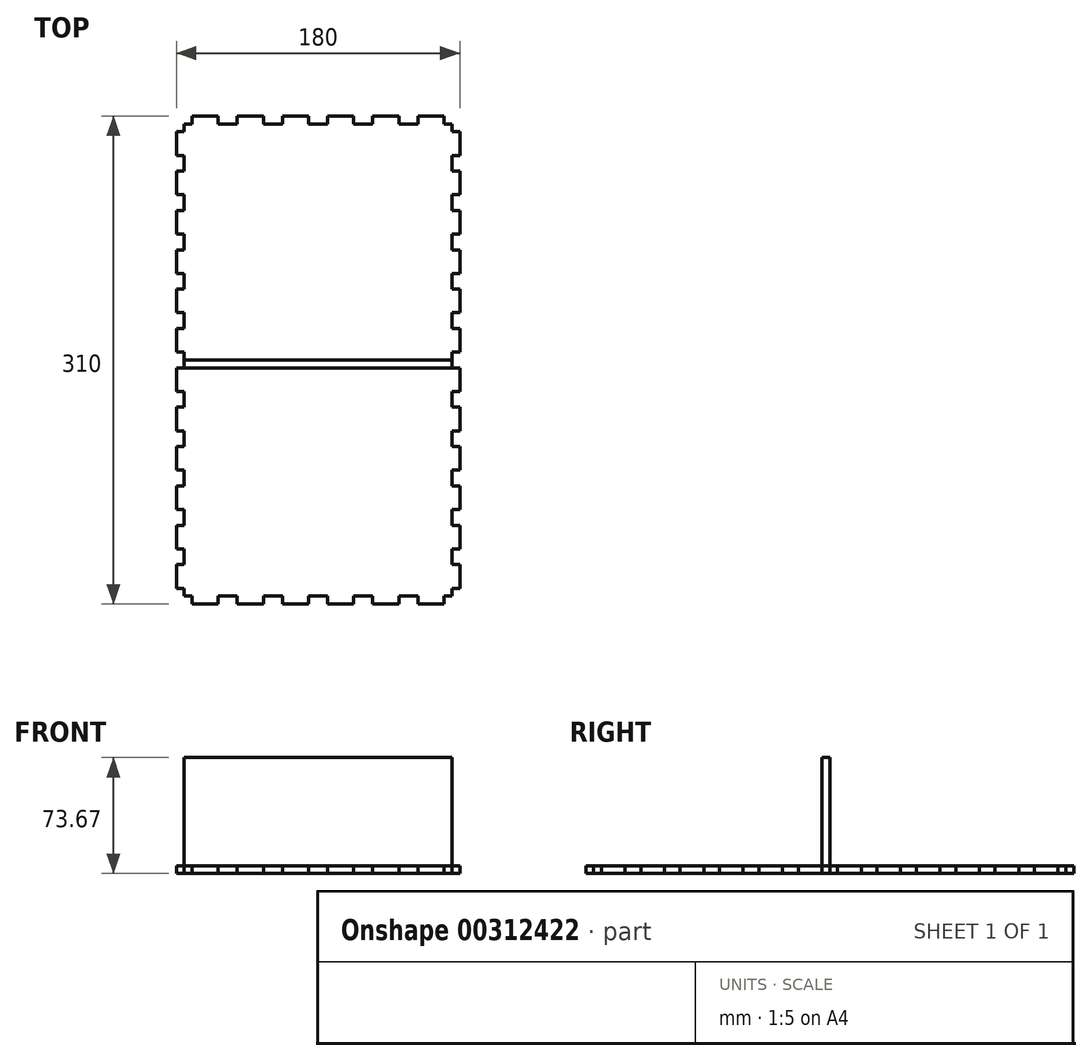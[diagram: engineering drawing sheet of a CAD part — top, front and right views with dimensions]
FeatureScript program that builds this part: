
annotation { "Feature Type Name" : "Feature", "Feature Type Description" : "" }
export const myFeature = defineFeature(function(context is Context, id is Id, definition is map)
    precondition{}
    {
        {
            assignVariable(context, id + "F0", {"name" : "Materialthickness", "anyValue" : 5});
        }
        {
            var Q0;
            Q0=qCreatedBy(makeId("Top.planeOp"),FACE);
            var sketch = newSketch(context, id + "F1", { "sketchPlane" : qUnion([Q0])});
            skLineSegment(sketch, "E0.top", {"start": v(-85, -150) * mm, "end": v(-80, -150) * mm});
            skLineSegment(sketch, "E0.left", {"start": v(-85, 150) * mm, "end": v(-85, 145) * mm});
            skLineSegment(sketch, "E0.right", {"start": v(85, 150) * mm, "end": v(85, 145) * mm});
            skLineSegment(sketch, "E1", {"start": v(0, 150) * mm, "end": v(0, -150) * mm, "construction": true});
            skLineSegment(sketch, "E2", {"start": v(-85, 0) * mm, "end": v(85, 0) * mm, "construction": true});
            skPoint(sketch, "E3", {"position": v(0, 0) * mm});
            skLineSegment(sketch, "E4.bottom", {"start": v(85, 145) * mm, "end": v(90, 145) * mm});
            skLineSegment(sketch, "E4.top", {"start": v(85, 130) * mm, "end": v(90, 130) * mm});
            skLineSegment(sketch, "E4.right", {"start": v(90, 145) * mm, "end": v(90, 130) * mm});
            skLineSegment(sketch, "E5.0.1.0", {"start": v(85, 120) * mm, "end": v(90, 120) * mm});
            skLineSegment(sketch, "E5.0.1.1", {"start": v(85, 105) * mm, "end": v(90, 105) * mm});
            skLineSegment(sketch, "E5.0.1.2", {"start": v(90, 120) * mm, "end": v(90, 105) * mm});
            skLineSegment(sketch, "E5.0.2.0", {"start": v(85, 95) * mm, "end": v(90, 95) * mm});
            skLineSegment(sketch, "E5.0.2.1", {"start": v(85, 80) * mm, "end": v(90, 80) * mm});
            skLineSegment(sketch, "E5.0.2.2", {"start": v(90, 95) * mm, "end": v(90, 80) * mm});
            skLineSegment(sketch, "E5.0.3.0", {"start": v(85, 70) * mm, "end": v(90, 70) * mm});
            skLineSegment(sketch, "E5.0.3.1", {"start": v(85, 55) * mm, "end": v(90, 55) * mm});
            skLineSegment(sketch, "E5.0.3.2", {"start": v(90, 70) * mm, "end": v(90, 55) * mm});
            skLineSegment(sketch, "E5.0.4.0", {"start": v(85, 45) * mm, "end": v(90, 45) * mm});
            skLineSegment(sketch, "E5.0.4.1", {"start": v(85, 30) * mm, "end": v(90, 30) * mm});
            skLineSegment(sketch, "E5.0.4.2", {"start": v(90, 45) * mm, "end": v(90, 30) * mm});
            skLineSegment(sketch, "E5.0.5.0", {"start": v(85, 20) * mm, "end": v(90, 20) * mm});
            skLineSegment(sketch, "E5.0.5.1", {"start": v(85, 5) * mm, "end": v(90, 5) * mm});
            skLineSegment(sketch, "E5.0.5.2", {"start": v(90, 20) * mm, "end": v(90, 5) * mm});
            skLineSegment(sketch, "E5.0.6.0", {"start": v(85, -5) * mm, "end": v(90, -5) * mm});
            skLineSegment(sketch, "E5.0.6.1", {"start": v(85, -20) * mm, "end": v(90, -20) * mm});
            skLineSegment(sketch, "E5.0.6.2", {"start": v(90, -5) * mm, "end": v(90, -20) * mm});
            skLineSegment(sketch, "E5.0.7.0", {"start": v(85, -30) * mm, "end": v(90, -30) * mm});
            skLineSegment(sketch, "E5.0.7.1", {"start": v(85, -45) * mm, "end": v(90, -45) * mm});
            skLineSegment(sketch, "E5.0.7.2", {"start": v(90, -30) * mm, "end": v(90, -45) * mm});
            skLineSegment(sketch, "E5.0.8.0", {"start": v(85, -55) * mm, "end": v(90, -55) * mm});
            skLineSegment(sketch, "E5.0.8.1", {"start": v(85, -70) * mm, "end": v(90, -70) * mm});
            skLineSegment(sketch, "E5.0.8.2", {"start": v(90, -55) * mm, "end": v(90, -70) * mm});
            skLineSegment(sketch, "E5.0.9.0", {"start": v(85, -80) * mm, "end": v(90, -80) * mm});
            skLineSegment(sketch, "E5.0.9.1", {"start": v(85, -95) * mm, "end": v(90, -95) * mm});
            skLineSegment(sketch, "E5.0.9.2", {"start": v(90, -80) * mm, "end": v(90, -95) * mm});
            skLineSegment(sketch, "E5.0.10.0", {"start": v(85, -105) * mm, "end": v(90, -105) * mm});
            skLineSegment(sketch, "E5.0.10.1", {"start": v(85, -120) * mm, "end": v(90, -120) * mm});
            skLineSegment(sketch, "E5.0.10.2", {"start": v(90, -105) * mm, "end": v(90, -120) * mm});
            skLineSegment(sketch, "E5.0.11.0", {"start": v(85, -130) * mm, "end": v(90, -130) * mm});
            skLineSegment(sketch, "E5.0.11.1", {"start": v(85, -145) * mm, "end": v(90, -145) * mm});
            skLineSegment(sketch, "E5.0.11.2", {"start": v(90, -130) * mm, "end": v(90, -145) * mm});
            skLineSegment(sketch, "E5.direction1", {"start": v(85, 130) * mm, "end": v(110, 130) * mm, "construction": true});
            skLineSegment(sketch, "E5.direction2", {"start": v(85, 130) * mm, "end": v(85, 120) * mm, "construction": true});
            skLineSegment(sketch, "E6.MirrorCS", {"start": v(-85, 130) * mm, "end": v(-90, 130) * mm});
            skLineSegment(sketch, "E7.MirrorCS", {"start": v(-85, -145) * mm, "end": v(-90, -145) * mm});
            skLineSegment(sketch, "E8.MirrorCS", {"start": v(-85, -130) * mm, "end": v(-90, -130) * mm});
            skLineSegment(sketch, "E9.MirrorCS", {"start": v(-85, 120) * mm, "end": v(-90, 120) * mm});
            skLineSegment(sketch, "E10.MirrorCS", {"start": v(-85, -30) * mm, "end": v(-90, -30) * mm});
            skLineSegment(sketch, "E11.MirrorCS", {"start": v(-85, 145) * mm, "end": v(-90, 145) * mm});
            skLineSegment(sketch, "E12.MirrorCS", {"start": v(-85, 70) * mm, "end": v(-90, 70) * mm});
            skLineSegment(sketch, "E13.MirrorCS", {"start": v(-85, 30) * mm, "end": v(-90, 30) * mm});
            skLineSegment(sketch, "E14.MirrorCS", {"start": v(-85, -105) * mm, "end": v(-90, -105) * mm});
            skLineSegment(sketch, "E15.MirrorCS", {"start": v(-85, 20) * mm, "end": v(-90, 20) * mm});
            skLineSegment(sketch, "E16.MirrorCS", {"start": v(-85, -20) * mm, "end": v(-90, -20) * mm});
            skLineSegment(sketch, "E17.MirrorCS", {"start": v(-85, 105) * mm, "end": v(-90, 105) * mm});
            skLineSegment(sketch, "E18.MirrorCS", {"start": v(-85, 5) * mm, "end": v(-90, 5) * mm});
            skLineSegment(sketch, "E19.MirrorCS", {"start": v(-85, -45) * mm, "end": v(-90, -45) * mm});
            skLineSegment(sketch, "E20.MirrorCS", {"start": v(-85, -120) * mm, "end": v(-90, -120) * mm});
            skLineSegment(sketch, "E21.MirrorCS", {"start": v(-85, -80) * mm, "end": v(-90, -80) * mm});
            skLineSegment(sketch, "E22.MirrorCS", {"start": v(-85, 55) * mm, "end": v(-90, 55) * mm});
            skLineSegment(sketch, "E23.MirrorCS", {"start": v(-85, -95) * mm, "end": v(-90, -95) * mm});
            skLineSegment(sketch, "E24.MirrorCS", {"start": v(-85, -70) * mm, "end": v(-90, -70) * mm});
            skLineSegment(sketch, "E25.MirrorCS", {"start": v(-85, -5) * mm, "end": v(-90, -5) * mm});
            skLineSegment(sketch, "E26.MirrorCS", {"start": v(-85, 45) * mm, "end": v(-90, 45) * mm});
            skLineSegment(sketch, "E27.MirrorCS", {"start": v(-85, 80) * mm, "end": v(-90, 80) * mm});
            skLineSegment(sketch, "E28.MirrorCS", {"start": v(-85, -55) * mm, "end": v(-90, -55) * mm});
            skLineSegment(sketch, "E29.MirrorCS", {"start": v(-85, 95) * mm, "end": v(-90, 95) * mm});
            skLineSegment(sketch, "E30.MirrorCS", {"start": v(-85, 130) * mm, "end": v(-85, 120) * mm, "construction": true});
            skLineSegment(sketch, "E31.MirrorCS", {"start": v(85, -150) * mm, "end": v(80, -150) * mm});
            skLineSegment(sketch, "E32.MirrorCS", {"start": v(-90, -30) * mm, "end": v(-90, -45) * mm});
            skLineSegment(sketch, "E33.MirrorCS", {"start": v(-85, 130) * mm, "end": v(-110, 130) * mm, "construction": true});
            skLineSegment(sketch, "E34.MirrorCS", {"start": v(85, 0) * mm, "end": v(-85, 0) * mm, "construction": true});
            skLineSegment(sketch, "E35.MirrorCS", {"start": v(-90, 145) * mm, "end": v(-90, 130) * mm});
            skLineSegment(sketch, "E36.MirrorCS", {"start": v(-90, 20) * mm, "end": v(-90, 5) * mm});
            skLineSegment(sketch, "E37.MirrorCS", {"start": v(-90, -130) * mm, "end": v(-90, -145) * mm});
            skLineSegment(sketch, "E38.MirrorCS", {"start": v(-90, -5) * mm, "end": v(-90, -20) * mm});
            skLineSegment(sketch, "E39.MirrorCS", {"start": v(-90, -105) * mm, "end": v(-90, -120) * mm});
            skLineSegment(sketch, "E40.MirrorCS", {"start": v(-90, 45) * mm, "end": v(-90, 30) * mm});
            skLineSegment(sketch, "E41.MirrorCS", {"start": v(-90, 120) * mm, "end": v(-90, 105) * mm});
            skLineSegment(sketch, "E42.MirrorCS", {"start": v(-90, 70) * mm, "end": v(-90, 55) * mm});
            skLineSegment(sketch, "E43.MirrorCS", {"start": v(-90, 95) * mm, "end": v(-90, 80) * mm});
            skLineSegment(sketch, "E44.MirrorCS", {"start": v(-90, -80) * mm, "end": v(-90, -95) * mm});
            skLineSegment(sketch, "E45.MirrorCS", {"start": v(-90, -55) * mm, "end": v(-90, -70) * mm});
            skLineSegment(sketch, "E46.trimOffspring", {"start": v(85, 130) * mm, "end": v(85, 120) * mm});
            skLineSegment(sketch, "E47.trimOffspring", {"start": v(85, 105) * mm, "end": v(85, 95) * mm});
            skLineSegment(sketch, "E48.trimOffspring", {"start": v(85, 80) * mm, "end": v(85, 70) * mm});
            skLineSegment(sketch, "E49.trimOffspring", {"start": v(85, 55) * mm, "end": v(85, 45) * mm});
            skLineSegment(sketch, "E50.trimOffspring", {"start": v(85, 30) * mm, "end": v(85, 20) * mm});
            skLineSegment(sketch, "E51.trimOffspring", {"start": v(85, -20) * mm, "end": v(85, -30) * mm});
            skLineSegment(sketch, "E52.trimOffspring", {"start": v(85, 5) * mm, "end": v(85, -5) * mm});
            skLineSegment(sketch, "E53.trimOffspring", {"start": v(85, -45) * mm, "end": v(85, -55) * mm});
            skLineSegment(sketch, "E54.trimOffspring", {"start": v(85, -70) * mm, "end": v(85, -80) * mm});
            skLineSegment(sketch, "E55.trimOffspring", {"start": v(85, -120) * mm, "end": v(85, -130) * mm});
            skLineSegment(sketch, "E56.trimOffspring", {"start": v(85, -145) * mm, "end": v(85, -150) * mm});
            skLineSegment(sketch, "E57.trimOffspring", {"start": v(-85, -145) * mm, "end": v(-85, -150) * mm});
            skLineSegment(sketch, "E58.trimOffspring", {"start": v(-85, -120) * mm, "end": v(-85, -130) * mm});
            skLineSegment(sketch, "E59.trimOffspring", {"start": v(-85, -95) * mm, "end": v(-85, -105) * mm});
            skLineSegment(sketch, "E60.trimOffspring", {"start": v(-85, -70) * mm, "end": v(-85, -80) * mm});
            skLineSegment(sketch, "E61.trimOffspring", {"start": v(-85, -45) * mm, "end": v(-85, -55) * mm});
            skLineSegment(sketch, "E62.trimOffspring", {"start": v(-85, -20) * mm, "end": v(-85, -30) * mm});
            skLineSegment(sketch, "E63.trimOffspring", {"start": v(-85, 5) * mm, "end": v(-85, -5) * mm});
            skLineSegment(sketch, "E64.trimOffspring", {"start": v(-85, 30) * mm, "end": v(-85, 20) * mm});
            skLineSegment(sketch, "E65.trimOffspring", {"start": v(-85, 55) * mm, "end": v(-85, 45) * mm});
            skLineSegment(sketch, "E66.trimOffspring", {"start": v(-85, 80) * mm, "end": v(-85, 70) * mm});
            skLineSegment(sketch, "E67.trimOffspring", {"start": v(-85, 105) * mm, "end": v(-85, 95) * mm});
            skLineSegment(sketch, "E68.trimOffspring", {"start": v(-85, 130) * mm, "end": v(-85, 120) * mm});
            skLineSegment(sketch, "E69", {"start": v(85, -95) * mm, "end": v(85, -105) * mm});
            skLineSegment(sketch, "E70", {"start": v(-85, 150) * mm, "end": v(-80, 150) * mm});
            skLineSegment(sketch, "E71.bottom", {"start": v(-80, 155) * mm, "end": v(-63.4, 155) * mm});
            skLineSegment(sketch, "E71.left", {"start": v(-80, 155) * mm, "end": v(-80, 150) * mm});
            skLineSegment(sketch, "E71.right", {"start": v(-63.4, 155) * mm, "end": v(-63.4, 150) * mm});
            skLineSegment(sketch, "E72.1.0.0", {"start": v(-51.32, 155) * mm, "end": v(-51.32, 150) * mm});
            skLineSegment(sketch, "E72.1.0.2", {"start": v(-34.73, 155) * mm, "end": v(-34.73, 150) * mm});
            skLineSegment(sketch, "E72.1.0.3", {"start": v(-51.32, 155) * mm, "end": v(-34.73, 155) * mm});
            skLineSegment(sketch, "E72.2.0.0", {"start": v(-22.64, 155) * mm, "end": v(-22.64, 150) * mm});
            skLineSegment(sketch, "E72.2.0.2", {"start": v(-6.04, 155) * mm, "end": v(-6.04, 150) * mm});
            skLineSegment(sketch, "E72.2.0.3", {"start": v(-22.64, 155) * mm, "end": v(-6.04, 155) * mm});
            skLineSegment(sketch, "E72.3.0.0", {"start": v(6.04, 155) * mm, "end": v(6.04, 150) * mm});
            skLineSegment(sketch, "E72.3.0.2", {"start": v(22.64, 155) * mm, "end": v(22.64, 150) * mm});
            skLineSegment(sketch, "E72.3.0.3", {"start": v(6.04, 155) * mm, "end": v(22.64, 155) * mm});
            skLineSegment(sketch, "E72.4.0.0", {"start": v(34.73, 155) * mm, "end": v(34.73, 150) * mm});
            skLineSegment(sketch, "E72.4.0.2", {"start": v(51.32, 155) * mm, "end": v(51.32, 150) * mm});
            skLineSegment(sketch, "E72.4.0.3", {"start": v(34.73, 155) * mm, "end": v(51.32, 155) * mm});
            skLineSegment(sketch, "E72.5.0.0", {"start": v(63.4, 155) * mm, "end": v(63.4, 150) * mm});
            skLineSegment(sketch, "E72.5.0.2", {"start": v(80, 155) * mm, "end": v(80, 150) * mm});
            skLineSegment(sketch, "E72.5.0.3", {"start": v(63.4, 155) * mm, "end": v(80, 155) * mm});
            skLineSegment(sketch, "E73.trimOffspring", {"start": v(-63.4, 150) * mm, "end": v(-51.32, 150) * mm});
            skLineSegment(sketch, "E74.trimOffspring", {"start": v(-34.73, 150) * mm, "end": v(-22.64, 150) * mm});
            skLineSegment(sketch, "E75.trimOffspring", {"start": v(-6.04, 150) * mm, "end": v(6.04, 150) * mm});
            skLineSegment(sketch, "E76.trimOffspring", {"start": v(22.64, 150) * mm, "end": v(34.73, 150) * mm});
            skLineSegment(sketch, "E77.trimOffspring", {"start": v(51.32, 150) * mm, "end": v(63.4, 150) * mm});
            skLineSegment(sketch, "E78.trimOffspring", {"start": v(80, 150) * mm, "end": v(85, 150) * mm});
            skLineSegment(sketch, "E79.MirrorCS", {"start": v(34.73, -155) * mm, "end": v(34.73, -150) * mm});
            skLineSegment(sketch, "E80.MirrorCS", {"start": v(51.32, -155) * mm, "end": v(51.32, -150) * mm});
            skLineSegment(sketch, "E81.MirrorCS", {"start": v(63.4, -155) * mm, "end": v(63.4, -150) * mm});
            skLineSegment(sketch, "E82.MirrorCS", {"start": v(80, -155) * mm, "end": v(80, -150) * mm});
            skLineSegment(sketch, "E83.MirrorCS", {"start": v(-80, -155) * mm, "end": v(-80, -150) * mm});
            skLineSegment(sketch, "E84.MirrorCS", {"start": v(-63.4, -155) * mm, "end": v(-63.4, -150) * mm});
            skLineSegment(sketch, "E85.MirrorCS", {"start": v(-51.32, -155) * mm, "end": v(-51.32, -150) * mm});
            skLineSegment(sketch, "E86.MirrorCS", {"start": v(-34.73, -155) * mm, "end": v(-34.73, -150) * mm});
            skLineSegment(sketch, "E87.MirrorCS", {"start": v(6.04, -155) * mm, "end": v(6.04, -150) * mm});
            skLineSegment(sketch, "E88.MirrorCS", {"start": v(-22.64, -155) * mm, "end": v(-22.64, -150) * mm});
            skLineSegment(sketch, "E89.MirrorCS", {"start": v(-6.04, -155) * mm, "end": v(-6.04, -150) * mm});
            skLineSegment(sketch, "E90.MirrorCS", {"start": v(22.64, -155) * mm, "end": v(22.64, -150) * mm});
            skLineSegment(sketch, "E91.MirrorCS", {"start": v(-6.04, -150) * mm, "end": v(6.04, -150) * mm});
            skLineSegment(sketch, "E92.MirrorCS", {"start": v(34.73, -155) * mm, "end": v(51.32, -155) * mm});
            skLineSegment(sketch, "E93.MirrorCS", {"start": v(-80, -155) * mm, "end": v(-63.4, -155) * mm});
            skLineSegment(sketch, "E94.MirrorCS", {"start": v(63.4, -155) * mm, "end": v(80, -155) * mm});
            skLineSegment(sketch, "E95.MirrorCS", {"start": v(-63.4, -150) * mm, "end": v(-51.32, -150) * mm});
            skLineSegment(sketch, "E96.MirrorCS", {"start": v(-34.73, -150) * mm, "end": v(-22.64, -150) * mm});
            skLineSegment(sketch, "E97.MirrorCS", {"start": v(-22.64, -155) * mm, "end": v(-6.04, -155) * mm});
            skLineSegment(sketch, "E98.MirrorCS", {"start": v(22.64, -150) * mm, "end": v(34.73, -150) * mm});
            skLineSegment(sketch, "E99.MirrorCS", {"start": v(-51.32, -155) * mm, "end": v(-34.73, -155) * mm});
            skLineSegment(sketch, "E100.MirrorCS", {"start": v(51.32, -150) * mm, "end": v(63.4, -150) * mm});
            skLineSegment(sketch, "E101.MirrorCS", {"start": v(6.04, -155) * mm, "end": v(22.64, -155) * mm});
            skLineSegment(sketch, "E102.trimOffspring", {"start": v(-80, -150) * mm, "end": v(-85, -150) * mm});
            skLineSegment(sketch, "E103.trimOffspring", {"start": v(-51.32, -150) * mm, "end": v(-63.4, -150) * mm});
            skLineSegment(sketch, "E104.trimOffspring", {"start": v(-22.64, -150) * mm, "end": v(-34.73, -150) * mm});
            skLineSegment(sketch, "E105.trimOffspring", {"start": v(6.04, -150) * mm, "end": v(-6.04, -150) * mm});
            skLineSegment(sketch, "E106.trimOffspring", {"start": v(80, -150) * mm, "end": v(85, -150) * mm});
            skLineSegment(sketch, "E107.trimOffspring", {"start": v(34.73, -150) * mm, "end": v(22.64, -150) * mm});
            skLineSegment(sketch, "E108.trimOffspring", {"start": v(63.4, -150) * mm, "end": v(51.32, -150) * mm});
            skSolve(sketch);
        }
        {
            var Q0;
            Q0 = qSketchRegion(id + "F1", true);
            extrude(context, id + "F2", {"entities" : qUnion([Q0]), "depth" : 5 * mm});
        }
        {
            var Q0;
            Q0=qCreatedBy(makeId("Front.planeOp"),FACE);
            var sketch = newSketch(context, id + "F3", { "sketchPlane" : qUnion([Q0])});
            skLineSegment(sketch, "E109.bottom", {"start": v(-85, 0) * mm, "end": v(85, 0) * mm});
            skLineSegment(sketch, "E109.top", {"start": v(-85, 73.67) * mm, "end": v(85, 73.67) * mm});
            skLineSegment(sketch, "E109.left", {"start": v(-85, 0) * mm, "end": v(-85, 73.67) * mm});
            skLineSegment(sketch, "E109.right", {"start": v(85, 0) * mm, "end": v(85, 73.67) * mm});
            skSolve(sketch);
        }
        {
            var Q0;
            {var subQ3=sQuery(id+"F3.wireOp",EDGE,"E109.top");Q0=makeQuery(id+"F3.imprint","IMPRINT",FACE,{"disambiguationData":[TD([[makeQuery(id+"F3.imprint","IMPRINT",EDGE,{"derivedFrom":subQ3}),-1.0]])]});}
            extrude(context, id + "F4", {"entities" : qUnion([Q0]), "depth" : (getVariable(context, 'Materialthickness')) * mm});
        }
    });
